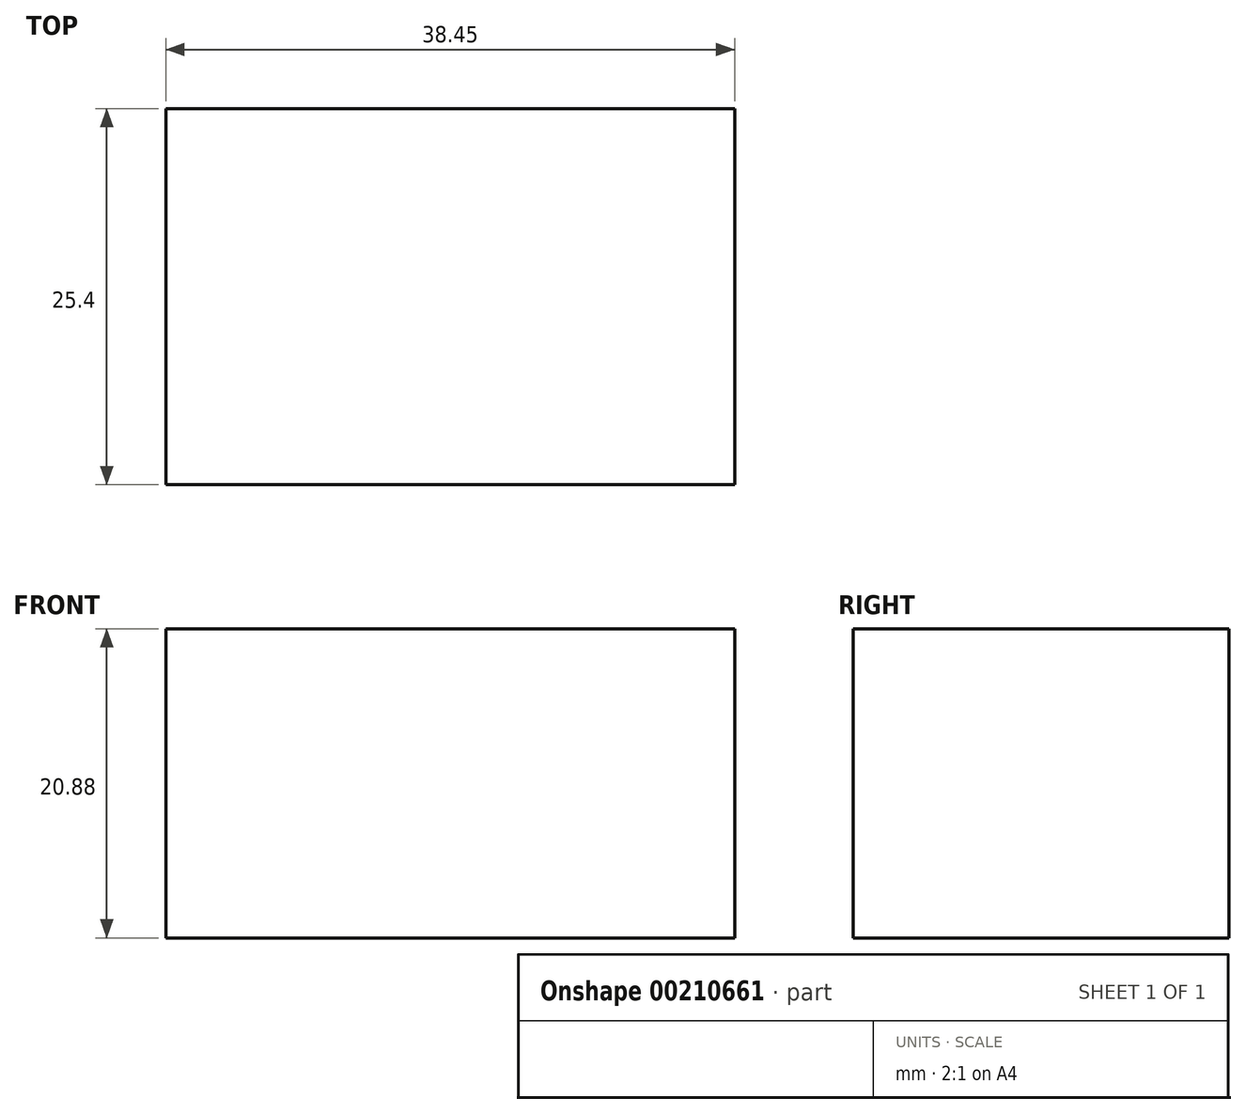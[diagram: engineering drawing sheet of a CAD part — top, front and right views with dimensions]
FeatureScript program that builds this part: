
annotation { "Feature Type Name" : "Feature", "Feature Type Description" : "" }
export const myFeature = defineFeature(function(context is Context, id is Id, definition is map)
    precondition{}
    {
        {
            var Q0;
            Q0=qCreatedBy(makeId("Front.planeOp"),FACE);
            var sketch = newSketch(context, id + "F0", { "sketchPlane" : qUnion([Q0])});
            skLineSegment(sketch, "E0.bottom", {"start": v(11.4, -54.27) * mm, "end": v(-27.05, -54.27) * mm});
            skLineSegment(sketch, "E0.top", {"start": v(11.4, -33.39) * mm, "end": v(-27.05, -33.39) * mm});
            skLineSegment(sketch, "E0.left", {"start": v(11.4, -54.27) * mm, "end": v(11.4, -33.39) * mm});
            skLineSegment(sketch, "E0.right", {"start": v(-27.05, -54.27) * mm, "end": v(-27.05, -33.39) * mm});
            skSolve(sketch);
        }
        {
            var Q0;
            Q0=makeQuery(id+"F0.imprint","IMPRINT",FACE,{"disambiguationData":[TD([[makeQuery(id+"F0.imprint","IMPRINT",EDGE,{"derivedFrom":sQuery(id+"F0.wireOp",EDGE,"E0.bottom")}),-1.0]])]});
            extrude(context, id + "F1", {"entities" : qUnion([Q0]), "depth" : 25.4 * mm});
        }
    });
